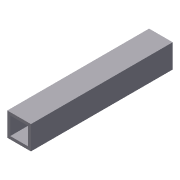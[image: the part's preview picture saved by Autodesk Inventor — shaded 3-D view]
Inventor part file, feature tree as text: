
AUTODESK INVENTOR PART (.ipt)
format: ipt  version: 2012 (Build 160160000, 160)  size: 71,680 bytes
history: native  units: in
note: dims shown in document units (in); Inventor stores cm internally (conversion verified against a paired STEP export)
features: extrude x1, shell x1, sketch x1
ambient origin geometry x8: Origin, YZ Plane, XZ Plane, XY Plane, X Axis, Y Axis, Z Axis, Center Point
bodies: Solid1 (feature_tree)
feature tree (3):
  extrude  "Extrusion1"  Depth=1.0in
  shell  "Shell1"  Thickness=6.0in
  sketch  "Sketch1"  dims[d0=1.0in d1=1.0in d2=6.0in d3=0.0in d4=0.125in]
